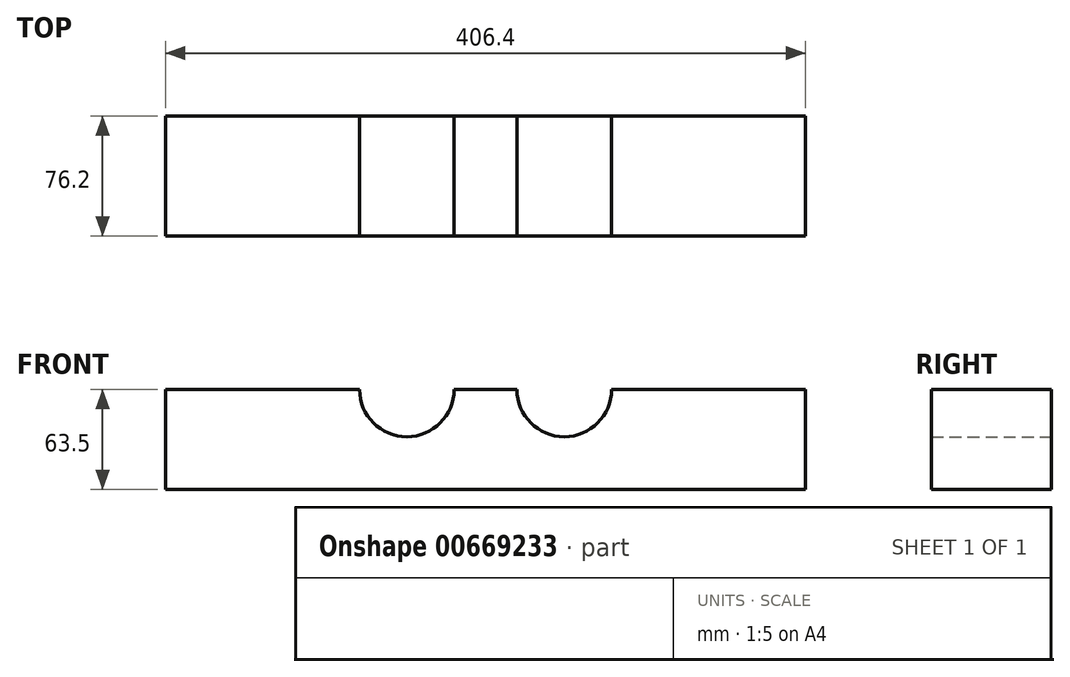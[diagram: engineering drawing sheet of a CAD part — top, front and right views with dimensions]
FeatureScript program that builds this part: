
annotation { "Feature Type Name" : "Feature", "Feature Type Description" : "" }
export const myFeature = defineFeature(function(context is Context, id is Id, definition is map)
    precondition{}
    {
        {
            var Q0;
            Q0=qCreatedBy(makeId("Front.planeOp"),FACE);
            var sketch = newSketch(context, id + "F0", { "sketchPlane" : qUnion([Q0])});
            skLineSegment(sketch, "E0.bottom", {"start": v(0, 0) * mm, "end": v(-203.2, 0) * mm});
            skLineSegment(sketch, "E0.top", {"start": v(0, 63.5) * mm, "end": v(-20, 63.5) * mm});
            skLineSegment(sketch, "E0.right", {"start": v(-203.2, 0) * mm, "end": v(-203.2, 63.5) * mm});
            skArc(sketch, "E1", {"start": v(-80, 63.5) * mm, "mid": v(-50, 33.5) * mm, "end": v(-20, 63.5) * mm});
            skLineSegment(sketch, "E2.trimOffspring", {"start": v(-80, 63.5) * mm, "end": v(-203.2, 63.5) * mm});
            skLineSegment(sketch, "E3.MirrorCS", {"start": v(80, 63.5) * mm, "end": v(203.2, 63.5) * mm});
            skLineSegment(sketch, "E4.MirrorCS", {"start": v(0, 63.5) * mm, "end": v(20, 63.5) * mm});
            skArc(sketch, "E5.MirrorCS", {"start": v(80, 63.5) * mm, "mid": v(50, 33.5) * mm, "end": v(20, 63.5) * mm});
            skLineSegment(sketch, "E6.MirrorCS", {"start": v(203.2, 0) * mm, "end": v(203.2, 63.5) * mm});
            skLineSegment(sketch, "E7.MirrorCS", {"start": v(0, 0) * mm, "end": v(203.2, 0) * mm});
            skSolve(sketch);
        }
        {
            var Q0;
            Q0 = qSketchRegion(id + "F0", true);
            extrude(context, id + "F1", {"entities" : qUnion([Q0]), "depth" : 76.2 * mm, "offsetDistance" : 25.4 * mm});
        }
    });
